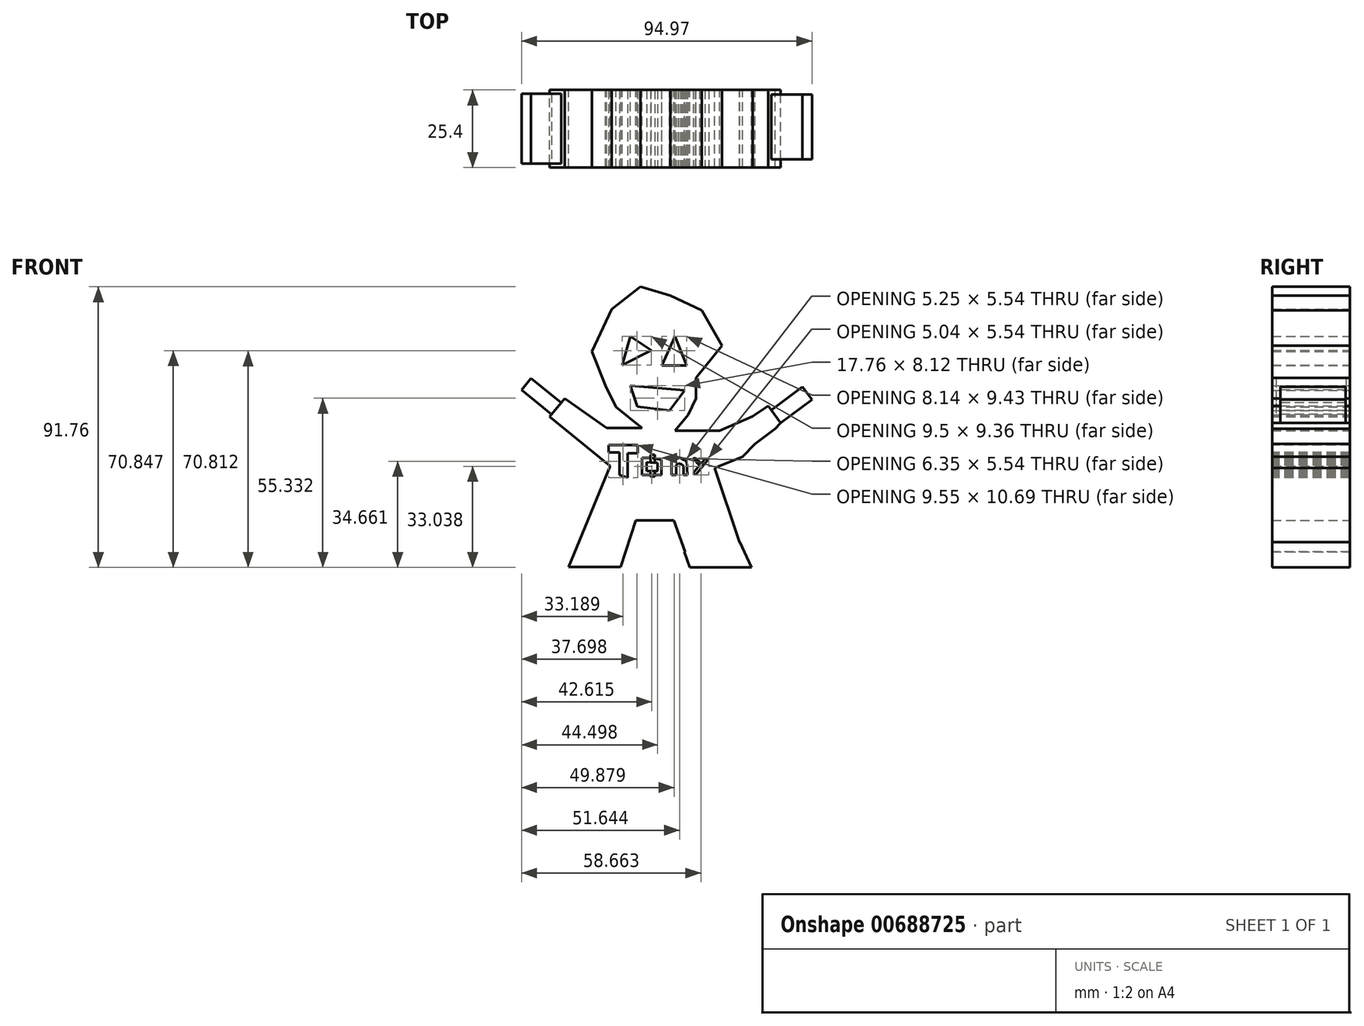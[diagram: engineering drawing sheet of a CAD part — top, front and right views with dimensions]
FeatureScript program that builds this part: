
annotation { "Feature Type Name" : "Feature", "Feature Type Description" : "" }
export const myFeature = defineFeature(function(context is Context, id is Id, definition is map)
    precondition{}
    {
        {
            var Q0;
            Q0=qCreatedBy(makeId("Front.planeOp"),FACE);
            var sketch = newSketch(context, id + "F0", { "sketchPlane" : qUnion([Q0])});
            skLineSegment(sketch, "E0.bottom", {"start": v(-60.07, 58.54) * mm, "end": v(66.93, 58.54) * mm});
            skLineSegment(sketch, "E0.top", {"start": v(-60.07, -68.46) * mm, "end": v(66.93, -68.46) * mm});
            skLineSegment(sketch, "E0.left", {"start": v(-60.07, 58.54) * mm, "end": v(-60.07, -68.46) * mm});
            skLineSegment(sketch, "E0.right", {"start": v(66.93, 58.54) * mm, "end": v(66.93, -68.46) * mm});
            skSolve(sketch);
        }
        {
            var Q0;
            Q0=makeQuery(id+"F0.imprint","IMPRINT",FACE,{"disambiguationData":[TD([[makeQuery(id+"F0.imprint","IMPRINT",EDGE,{"derivedFrom":sQuery(id+"F0.wireOp",EDGE,"E0.bottom")}),-1.0]])]});
            extrude(context, id + "F1", {"entities" : qUnion([Q0]), "depth" : 25.4 * mm, "offsetDistance" : 25.4 * mm});
        }
        {
            var Q0;
            Q0=makeQuery(id+"F1.opExtrude","CAP_FACE",FACE,{"disambiguationData":[OSD([sQuery(id+"F0.wireOp",EDGE,"E0.bottom"),sQuery(id+"F0.wireOp",EDGE,"E0.top"),sQuery(id+"F0.wireOp",EDGE,"E0.left"),sQuery(id+"F0.wireOp",EDGE,"E0.right")])],"isStart":false});
            var sketch = newSketch(context, id + "F2", { "sketchPlane" : qUnion([Q0])});
            skLineSegment(sketch, "E1", {"start": v(-30.9, -68.46) * mm, "end": v(-13.51, -26.26) * mm});
            skLineSegment(sketch, "E2", {"start": v(-13.51, -26.26) * mm, "end": v(-39.68, -4.87) * mm});
            skLineSegment(sketch, "E3", {"start": v(-39.68, -4.87) * mm, "end": v(-34.33, 0) * mm});
            skLineSegment(sketch, "E4", {"start": v(-34.33, 0) * mm, "end": v(-34.33, 2.58) * mm});
            skLineSegment(sketch, "E5", {"start": v(-34.33, 2.58) * mm, "end": v(-34.33, 6.2) * mm});
            skLineSegment(sketch, "E6", {"start": v(-34.33, 6.2) * mm, "end": v(-43.69, 6.2) * mm});
            skLineSegment(sketch, "E7", {"start": v(-43.69, 6.2) * mm, "end": v(-45.02, -5.82) * mm});
            skLineSegment(sketch, "E8", {"start": v(-45.02, -5.82) * mm, "end": v(-39.68, -6.02) * mm});
            skLineSegment(sketch, "E9", {"start": v(-34.33, 0) * mm, "end": v(-14.66, -13.84) * mm});
            skLineSegment(sketch, "E10", {"start": v(-14.66, -13.84) * mm, "end": v(-3.01, -13.84) * mm});
            skLineSegment(sketch, "E11", {"start": v(-3.01, -13.84) * mm, "end": v(-11.53, -6.88) * mm});
            skLineSegment(sketch, "E12", {"start": v(-11.53, -6.88) * mm, "end": v(-15.04, 0) * mm});
            skLineSegment(sketch, "E13", {"start": v(-15.04, 0) * mm, "end": v(-19.43, 11.17) * mm});
            skLineSegment(sketch, "E14", {"start": v(-19.43, 11.17) * mm, "end": v(-12.94, 25.11) * mm});
            skLineSegment(sketch, "E15", {"start": v(-12.94, 25.11) * mm, "end": v(-3.58, 32.37) * mm});
            skLineSegment(sketch, "E16", {"start": v(-3.58, 32.37) * mm, "end": v(6.15, 29.5) * mm});
            skLineSegment(sketch, "E17", {"start": v(6.15, 29.5) * mm, "end": v(16.48, 24.7) * mm});
            skLineSegment(sketch, "E18", {"start": v(16.48, 24.7) * mm, "end": v(23.15, 13.08) * mm});
            skLineSegment(sketch, "E19", {"start": v(23.15, 13.08) * mm, "end": v(14.54, 2.55) * mm});
            skLineSegment(sketch, "E20", {"start": v(14.54, 2.55) * mm, "end": v(14.54, -4.1) * mm});
            skLineSegment(sketch, "E21", {"start": v(14.54, -4.1) * mm, "end": v(12.02, -9.53) * mm});
            skLineSegment(sketch, "E22", {"start": v(12.02, -9.53) * mm, "end": v(7.75, -14.75) * mm});
            skLineSegment(sketch, "E23", {"start": v(7.75, -14.75) * mm, "end": v(22.38, -14.75) * mm});
            skLineSegment(sketch, "E24", {"start": v(22.38, -14.75) * mm, "end": v(33.08, -10.03) * mm});
            skLineSegment(sketch, "E25", {"start": v(33.08, -10.03) * mm, "end": v(38.23, -6.59) * mm});
            skLineSegment(sketch, "E26", {"start": v(38.23, -6.59) * mm, "end": v(41.35, -2.77) * mm});
            skLineSegment(sketch, "E27", {"start": v(41.35, -2.77) * mm, "end": v(41.29, 0) * mm});
            skLineSegment(sketch, "E28", {"start": v(41.29, 0) * mm, "end": v(45.32, 4.93) * mm});
            skLineSegment(sketch, "E29", {"start": v(45.32, 4.93) * mm, "end": v(50.4, 2.55) * mm});
            skLineSegment(sketch, "E30", {"start": v(50.4, 2.55) * mm, "end": v(51.6, -3.53) * mm});
            skLineSegment(sketch, "E31", {"start": v(51.6, -3.53) * mm, "end": v(50.65, -6.02) * mm});
            skLineSegment(sketch, "E32", {"start": v(50.65, -6.02) * mm, "end": v(45.87, -6.02) * mm});
            skLineSegment(sketch, "E33", {"start": v(45.87, -6.02) * mm, "end": v(43.78, -10.51) * mm});
            skLineSegment(sketch, "E34", {"start": v(43.78, -10.51) * mm, "end": v(40.53, -14.04) * mm});
            skLineSegment(sketch, "E35", {"start": v(40.53, -14.04) * mm, "end": v(33.84, -19) * mm});
            skLineSegment(sketch, "E36", {"start": v(33.84, -19) * mm, "end": v(29.83, -23.2) * mm});
            skLineSegment(sketch, "E37", {"start": v(29.83, -23.2) * mm, "end": v(20.67, -26.83) * mm});
            skLineSegment(sketch, "E38", {"start": v(20.67, -26.83) * mm, "end": v(34.6, -68.46) * mm});
            skLineSegment(sketch, "E39", {"start": v(34.6, -68.46) * mm, "end": v(16.27, -68.46) * mm});
            skLineSegment(sketch, "E40", {"start": v(16.27, -68.46) * mm, "end": v(7.3, -44.02) * mm});
            skLineSegment(sketch, "E41", {"start": v(7.3, -44.02) * mm, "end": v(-5.11, -44.02) * mm});
            skLineSegment(sketch, "E42", {"start": v(-5.11, -44.02) * mm, "end": v(-12.94, -68.46) * mm});
            skLineSegment(sketch, "E43", {"start": v(-12.94, -68.46) * mm, "end": v(-30.9, -68.46) * mm});
            skLineSegment(sketch, "E44", {"start": v(-33.24, -10.13) * mm, "end": v(-28.38, -4.19) * mm});
            skLineSegment(sketch, "E45", {"start": v(38.23, -6.59) * mm, "end": v(42.32, -12.09) * mm});
            skLineSegment(sketch, "E46", {"start": v(-27.12, -59.3) * mm, "end": v(-10, -59.3) * mm});
            skLineSegment(sketch, "E47", {"start": v(11.14, -54.46) * mm, "end": v(28.87, -51.34) * mm});
            skLineSegment(sketch, "E48", {"start": v(-19.2, -40.09) * mm, "end": v(25.1, -40.09) * mm});
            skLineSegment(sketch, "E49", {"start": v(-3.01, -13.84) * mm, "end": v(0, -18.8) * mm});
            skLineSegment(sketch, "E50", {"start": v(0, -18.8) * mm, "end": v(4.63, -18.8) * mm});
            skLineSegment(sketch, "E51", {"start": v(4.63, -18.8) * mm, "end": v(7.75, -14.75) * mm});
            skLineSegment(sketch, "E52", {"start": v(-6.83, 16.14) * mm, "end": v(-9.5, 6.78) * mm});
            skLineSegment(sketch, "E53", {"start": v(-9.5, 6.78) * mm, "end": v(0, 11.63) * mm});
            skLineSegment(sketch, "E54", {"start": v(0, 11.63) * mm, "end": v(-6.83, 16.14) * mm});
            skLineSegment(sketch, "E55", {"start": v(7.75, 16.14) * mm, "end": v(3.36, 6.7) * mm});
            skLineSegment(sketch, "E56", {"start": v(3.36, 6.7) * mm, "end": v(11.5, 6.7) * mm});
            skLineSegment(sketch, "E57", {"start": v(11.5, 6.7) * mm, "end": v(7.75, 16.14) * mm});
            skLineSegment(sketch, "E58", {"start": v(-6.83, 0) * mm, "end": v(10.93, -1.43) * mm});
            skLineSegment(sketch, "E59", {"start": v(10.93, -1.43) * mm, "end": v(5.96, -8.12) * mm});
            skLineSegment(sketch, "E60", {"start": v(5.96, -8.12) * mm, "end": v(-4.54, -6.78) * mm});
            skLineSegment(sketch, "E61", {"start": v(-4.54, -6.78) * mm, "end": v(-6.83, 0) * mm});
            skLineSegment(sketch, "E62", {"start": v(-9.5, -22.06) * mm, "end": v(-9.5, -33.51) * mm});
            skLineSegment(sketch, "E63", {"start": v(-9.5, -33.51) * mm, "end": v(-9.5, -22.06) * mm});
            skLineSegment(sketch, "E64", {"start": v(-3.01, -22.06) * mm, "end": v(-15.8, -22.06) * mm});
            skLineSegment(sketch, "E65", {"start": v(1.95, -25.87) * mm, "end": v(-3.4, -25.87) * mm});
            skLineSegment(sketch, "E66", {"start": v(-3.4, -25.87) * mm, "end": v(-3.4, -32.75) * mm});
            skLineSegment(sketch, "E67", {"start": v(-3.4, -32.75) * mm, "end": v(1.76, -32.75) * mm});
            skLineSegment(sketch, "E68", {"start": v(1.76, -32.75) * mm, "end": v(1.95, -25.87) * mm});
            skLineSegment(sketch, "E69", {"start": v(5.96, -32.75) * mm, "end": v(5.96, -22.06) * mm});
            skLineSegment(sketch, "E70", {"start": v(5.96, -22.06) * mm, "end": v(10.35, -34.28) * mm});
            skLineSegment(sketch, "E71", {"start": v(10.35, -34.28) * mm, "end": v(10.35, -22.06) * mm});
            skLineSegment(sketch, "E72", {"start": v(14.17, -23.2) * mm, "end": v(16.64, -29.43) * mm});
            skLineSegment(sketch, "E73", {"start": v(16.64, -29.43) * mm, "end": v(19.14, -22.44) * mm});
            skLineSegment(sketch, "E74", {"start": v(19.14, -22.44) * mm, "end": v(16.64, -29.43) * mm});
            skLineSegment(sketch, "E75", {"start": v(16.64, -37.52) * mm, "end": v(16.64, -29.43) * mm});
            skSolve(sketch);
        }
        {
            var Q0;
            Q0=makeQuery(id+"F2.imprint","IMPRINT",FACE,{"disambiguationData":[TD([[makeQuery(id+"F2.imprint","IMPRINT",EDGE,{"derivedFrom":sQuery(id+"F2.wireOp",EDGE,"E11")}),-1.0]])]});
            var Q1;
            {var subQ7=sQuery(id+"F2.wireOp",EDGE,"E10");Q1=makeQuery(id+"F2.imprint","IMPRINT",FACE,{"disambiguationData":[TD([[makeQuery(id+"F2.imprint","IMPRINT",EDGE,{"derivedFrom":subQ7}),-1.0]])]});}
            var Q2;
            Q2=makeQuery(id+"F2.imprint","IMPRINT",FACE,{"disambiguationData":[TD([[makeQuery(id+"F2.imprint","IMPRINT",EDGE,{"derivedFrom":sQuery(id+"F2.wireOp",EDGE,"E65")}),1.0]])]});
            var Q3;
            {var subQ0=sQuery(id+"F2.wireOp",EDGE,"E41");Q3=makeQuery(id+"F2.imprint","IMPRINT",FACE,{"disambiguationData":[TD([[makeQuery(id+"F2.imprint","IMPRINT",EDGE,{"derivedFrom":subQ0}),-1.0]])]});}
            extrude(context, id + "F3", {"entities" : qUnion([Q0, Q1, Q2, Q3]), "operationType" : NewBodyOperationType.ADD, "depth" : 25.4 * mm, "offsetDistance" : 25.4 * mm});
        }
        {
            var Q0;
            {var subQ0=sQuery(id+"F0.wireOp",EDGE,"E0.top");var subQ1=sQuery(id+"F0.wireOp",EDGE,"E0.right");var subQ2=sQuery(id+"F0.wireOp",EDGE,"E0.bottom");var subQ3=sQuery(id+"F0.wireOp",EDGE,"E0.left");Q0=makeQuery(id+"F3.boolean.opBoolean","SPLIT",FACE,{"disambiguationData":[TD([makeQuery(id+"F1.opExtrude","SWEPT_FACE",FACE,{"disambiguationData":[OSD([subQ2])]})])],"derivedFrom":makeQuery(id+"F1.opExtrude","CAP_FACE",FACE,{"disambiguationData":[OSD([subQ2,subQ0,subQ3,subQ1])],"isStart":false})});}
            var sketch = newSketch(context, id + "F4", { "sketchPlane" : qUnion([Q0])});
            skLineSegment(sketch, "E76.bottom", {"start": v(-60.07, 58.54) * mm, "end": v(66.93, 58.54) * mm});
            skLineSegment(sketch, "E76.top", {"start": v(-60.07, -68.46) * mm, "end": v(66.93, -68.46) * mm});
            skLineSegment(sketch, "E76.left", {"start": v(-60.07, 58.54) * mm, "end": v(-60.07, -68.46) * mm});
            skLineSegment(sketch, "E76.right", {"start": v(66.93, 58.54) * mm, "end": v(66.93, -68.46) * mm});
            skSolve(sketch);
        }
        {
            var Q0;
            Q0 = qSketchRegion(id + "F4", true);
            extrude(context, id + "F5", {"entities" : qUnion([Q0]), "operationType" : NewBodyOperationType.REMOVE, "oppositeDirection" : true, "depth" : 25.4 * mm, "offsetDistance" : 25.4 * mm});
        }
        {
            var Q0;
            Q0=makeQuery(id+"F3.opExtrude","SWEPT_FACE",FACE,{"disambiguationData":[OSD([sQuery(id+"F2.wireOp",EDGE,"E44")])]});
            var sketch = newSketch(context, id + "F6", { "sketchPlane" : qUnion([Q0])});
            skSolve(sketch);
        }
        {
            var Q0;
            Q0=makeQuery(id+"F3.opExtrude","SWEPT_FACE",FACE,{"disambiguationData":[OSD([sQuery(id+"F2.wireOp",EDGE,"E45")])]});
            var sketch = newSketch(context, id + "F7", { "sketchPlane" : qUnion([Q0])});
            skLineSegment(sketch, "E77.bottom", {"start": v(-48.1, -29.78) * mm, "end": v(-26.82, -29.78) * mm});
            skLineSegment(sketch, "E77.top", {"start": v(-48.1, -34.94) * mm, "end": v(-26.82, -34.94) * mm});
            skLineSegment(sketch, "E77.left", {"start": v(-48.1, -29.78) * mm, "end": v(-48.1, -34.94) * mm});
            skLineSegment(sketch, "E77.right", {"start": v(-26.82, -29.78) * mm, "end": v(-26.82, -34.94) * mm});
            skSolve(sketch);
        }
        {
            var Q0;
            Q0 = qSketchRegion(id + "F7", true);
            extrude(context, id + "F8", {"entities" : qUnion([Q0]), "operationType" : NewBodyOperationType.ADD, "depth" : 12.7 * mm, "offsetDistance" : 25.4 * mm});
        }
        {
            var Q0;
            Q0=qCreatedBy(makeId("Front.planeOp"),FACE);
            var sketch = newSketch(context, id + "F9", { "sketchPlane" : qUnion([Q0])});
            skLineSegment(sketch, "E78", {"start": v(10.79, -54.35) * mm, "end": v(12.6, -59.4) * mm});
            skLineSegment(sketch, "E79", {"start": v(12.6, -59.4) * mm, "end": v(32.76, -59.4) * mm});
            skLineSegment(sketch, "E80", {"start": v(32.76, -59.4) * mm, "end": v(28.93, -51.13) * mm});
            skLineSegment(sketch, "E81", {"start": v(28.93, -51.13) * mm, "end": v(10.79, -54.35) * mm});
            skSolve(sketch);
        }
        {
            var Q0;
            Q0=makeQuery(id+"F9.imprint","IMPRINT",FACE,{"disambiguationData":[TD([[makeQuery(id+"F9.imprint","IMPRINT",EDGE,{"derivedFrom":sQuery(id+"F9.wireOp",EDGE,"E78")}),1.0]])]});
            extrude(context, id + "F10", {"entities" : qUnion([Q0]), "operationType" : NewBodyOperationType.ADD, "depth" : 50.8 * mm, "offsetDistance" : 25.4 * mm});
        }
        {
            var Q0;
            Q0=makeQuery(id+"F10.opExtrude","CAP_FACE",FACE,{"disambiguationData":[OSD([sQuery(id+"F9.wireOp",EDGE,"E78"),sQuery(id+"F9.wireOp",EDGE,"E79"),sQuery(id+"F9.wireOp",EDGE,"E80"),sQuery(id+"F9.wireOp",EDGE,"E81")])],"isStart":true});
            extrude(context, id + "F11", {"entities" : qUnion([Q0]), "operationType" : NewBodyOperationType.REMOVE, "oppositeDirection" : true, "depth" : 25.4 * mm, "offsetDistance" : 25.4 * mm});
        }
        {
            var Q0;
            Q0=makeQuery(id+"F10.boolean.opBoolean","MERGE",FACE,{"derivedFrom":[makeQuery(id+"F3.opExtrude","CAP_FACE",FACE,{"disambiguationData":[OSD([sQuery(id+"F2.wireOp",EDGE,"E1"),sQuery(id+"F2.wireOp",EDGE,"E2"),sQuery(id+"F2.wireOp",EDGE,"E9"),sQuery(id+"F2.wireOp",EDGE,"E10"),sQuery(id+"F2.wireOp",EDGE,"E11"),sQuery(id+"F2.wireOp",EDGE,"E12"),sQuery(id+"F2.wireOp",EDGE,"E13"),sQuery(id+"F2.wireOp",EDGE,"E14"),sQuery(id+"F2.wireOp",EDGE,"E15"),sQuery(id+"F2.wireOp",EDGE,"E16"),sQuery(id+"F2.wireOp",EDGE,"E17"),sQuery(id+"F2.wireOp",EDGE,"E18"),sQuery(id+"F2.wireOp",EDGE,"E19"),sQuery(id+"F2.wireOp",EDGE,"E20"),sQuery(id+"F2.wireOp",EDGE,"E21"),sQuery(id+"F2.wireOp",EDGE,"E22"),sQuery(id+"F2.wireOp",EDGE,"E23"),sQuery(id+"F2.wireOp",EDGE,"E24"),sQuery(id+"F2.wireOp",EDGE,"E25"),sQuery(id+"F2.wireOp",EDGE,"E34"),sQuery(id+"F2.wireOp",EDGE,"E35"),sQuery(id+"F2.wireOp",EDGE,"E36"),sQuery(id+"F2.wireOp",EDGE,"E37"),sQuery(id+"F2.wireOp",EDGE,"E38"),sQuery(id+"F2.wireOp",EDGE,"E40"),sQuery(id+"F2.wireOp",EDGE,"E41"),sQuery(id+"F2.wireOp",EDGE,"E42"),sQuery(id+"F2.wireOp",EDGE,"E44"),sQuery(id+"F2.wireOp",EDGE,"E45"),sQuery(id+"F2.wireOp",EDGE,"E46"),sQuery(id+"F2.wireOp",EDGE,"E47"),sQuery(id+"F2.wireOp",EDGE,"E52"),sQuery(id+"F2.wireOp",EDGE,"E53"),sQuery(id+"F2.wireOp",EDGE,"E54"),sQuery(id+"F2.wireOp",EDGE,"E55"),sQuery(id+"F2.wireOp",EDGE,"E56"),sQuery(id+"F2.wireOp",EDGE,"E57"),sQuery(id+"F2.wireOp",EDGE,"E58"),sQuery(id+"F2.wireOp",EDGE,"E59"),sQuery(id+"F2.wireOp",EDGE,"E60"),sQuery(id+"F2.wireOp",EDGE,"E61")])],"isStart":false}),makeQuery(id+"F10.opExtrude","CAP_FACE",FACE,{"disambiguationData":[OSD([sQuery(id+"F9.wireOp",EDGE,"E78"),sQuery(id+"F9.wireOp",EDGE,"E79"),sQuery(id+"F9.wireOp",EDGE,"E80"),sQuery(id+"F9.wireOp",EDGE,"E81")])],"isStart":false})]});
            var sketch = newSketch(context, id + "F12", { "sketchPlane" : qUnion([Q0])});
            skLineSegment(sketch, "E82", {"start": v(-10.4, -29.12) * mm, "end": v(-10.4, -21.86) * mm});
            skLineSegment(sketch, "E83", {"start": v(-10.4, -21.86) * mm, "end": v(-14.04, -21.86) * mm});
            skLineSegment(sketch, "E84", {"start": v(-14.04, -21.86) * mm, "end": v(-14.04, -19.38) * mm});
            skLineSegment(sketch, "E85", {"start": v(-14.04, -19.38) * mm, "end": v(-4.49, -19.38) * mm});
            skLineSegment(sketch, "E86", {"start": v(-4.49, -19.38) * mm, "end": v(-4.49, -22.06) * mm});
            skLineSegment(sketch, "E87", {"start": v(-4.49, -22.06) * mm, "end": v(-7.73, -22.06) * mm});
            skLineSegment(sketch, "E88", {"start": v(-7.73, -22.06) * mm, "end": v(-7.73, -30.08) * mm});
            skLineSegment(sketch, "E89", {"start": v(-7.73, -30.08) * mm, "end": v(-10.4, -29.12) * mm});
            skLineSegment(sketch, "E90", {"start": v(0, -23.58) * mm, "end": v(-3.01, -23.58) * mm});
            skLineSegment(sketch, "E91", {"start": v(-3.01, -23.58) * mm, "end": v(-3.01, -29.12) * mm});
            skLineSegment(sketch, "E92", {"start": v(-3.01, -29.12) * mm, "end": v(3.34, -29.12) * mm});
            skLineSegment(sketch, "E93", {"start": v(3.34, -29.12) * mm, "end": v(3.34, -24.16) * mm});
            skLineSegment(sketch, "E94", {"start": v(3.34, -24.16) * mm, "end": v(0, -23.58) * mm});
            skLineSegment(sketch, "E95", {"start": v(-1.56, -24.96) * mm, "end": v(-1.56, -27.93) * mm});
            skLineSegment(sketch, "E96", {"start": v(-1.56, -27.93) * mm, "end": v(2, -27.93) * mm});
            skLineSegment(sketch, "E97", {"start": v(2, -27.93) * mm, "end": v(2, -25.29) * mm});
            skLineSegment(sketch, "E98", {"start": v(2, -25.29) * mm, "end": v(-1.56, -24.96) * mm});
            skLineSegment(sketch, "E99", {"start": v(6.57, -29.12) * mm, "end": v(6.57, -23.58) * mm});
            skLineSegment(sketch, "E100", {"start": v(6.57, -23.58) * mm, "end": v(7.56, -23.58) * mm});
            skLineSegment(sketch, "E101", {"start": v(7.56, -23.58) * mm, "end": v(7.56, -24.64) * mm});
            skLineSegment(sketch, "E102", {"start": v(7.56, -24.64) * mm, "end": v(8.02, -24.16) * mm});
            skLineSegment(sketch, "E103", {"start": v(8.02, -24.16) * mm, "end": v(8.78, -23.58) * mm});
            skLineSegment(sketch, "E104", {"start": v(8.78, -23.58) * mm, "end": v(9.55, -23.58) * mm});
            skLineSegment(sketch, "E105", {"start": v(9.55, -23.58) * mm, "end": v(10.32, -24.16) * mm});
            skLineSegment(sketch, "E106", {"start": v(10.32, -24.16) * mm, "end": v(11.03, -24.33) * mm});
            skLineSegment(sketch, "E107", {"start": v(11.03, -24.33) * mm, "end": v(11.48, -24.96) * mm});
            skLineSegment(sketch, "E108", {"start": v(11.48, -24.96) * mm, "end": v(11.68, -25.94) * mm});
            skLineSegment(sketch, "E109", {"start": v(11.68, -25.94) * mm, "end": v(11.68, -27.6) * mm});
            skLineSegment(sketch, "E110", {"start": v(11.68, -27.6) * mm, "end": v(11.82, -28.41) * mm});
            skLineSegment(sketch, "E111", {"start": v(11.82, -28.41) * mm, "end": v(11.82, -29.12) * mm});
            skLineSegment(sketch, "E112", {"start": v(11.82, -29.12) * mm, "end": v(10.57, -29.12) * mm});
            skLineSegment(sketch, "E113", {"start": v(10.57, -29.12) * mm, "end": v(10.57, -26.26) * mm});
            skLineSegment(sketch, "E114", {"start": v(10.57, -26.26) * mm, "end": v(9.8, -25.63) * mm});
            skLineSegment(sketch, "E115", {"start": v(9.8, -25.63) * mm, "end": v(8.81, -25.32) * mm});
            skLineSegment(sketch, "E116", {"start": v(8.81, -25.32) * mm, "end": v(8.16, -25.94) * mm});
            skLineSegment(sketch, "E117", {"start": v(8.16, -25.94) * mm, "end": v(8.16, -29.12) * mm});
            skLineSegment(sketch, "E118", {"start": v(8.16, -29.12) * mm, "end": v(6.57, -29.12) * mm});
            skLineSegment(sketch, "E119", {"start": v(13.7, -23.87) * mm, "end": v(15.68, -25.97) * mm});
            skLineSegment(sketch, "E120", {"start": v(15.68, -25.97) * mm, "end": v(13.7, -28.47) * mm});
            skLineSegment(sketch, "E121", {"start": v(13.7, -28.47) * mm, "end": v(14.51, -29.12) * mm});
            skLineSegment(sketch, "E122", {"start": v(14.51, -29.12) * mm, "end": v(18.73, -23.81) * mm});
            skLineSegment(sketch, "E123", {"start": v(18.73, -23.81) * mm, "end": v(17.53, -23.81) * mm});
            skLineSegment(sketch, "E124", {"start": v(17.53, -23.81) * mm, "end": v(16.4, -25.5) * mm});
            skLineSegment(sketch, "E125", {"start": v(16.4, -25.5) * mm, "end": v(14.35, -23.58) * mm});
            skLineSegment(sketch, "E126", {"start": v(14.35, -23.58) * mm, "end": v(13.7, -23.87) * mm});
            skSolve(sketch);
        }
        {
            var Q0;
            Q0=makeQuery(id+"F12.imprint","IMPRINT",FACE,{"disambiguationData":[TD([[makeQuery(id+"F12.imprint","IMPRINT",EDGE,{"derivedFrom":sQuery(id+"F12.wireOp",EDGE,"E82")}),-1.0]])]});
            var Q1;
            Q1=makeQuery(id+"F12.imprint","IMPRINT",FACE,{"disambiguationData":[TD([[makeQuery(id+"F12.imprint","IMPRINT",EDGE,{"derivedFrom":sQuery(id+"F12.wireOp",EDGE,"E90")}),1.0]])]});
            var Q2;
            Q2=makeQuery(id+"F12.imprint","IMPRINT",FACE,{"disambiguationData":[TD([[makeQuery(id+"F12.imprint","IMPRINT",EDGE,{"derivedFrom":sQuery(id+"F12.wireOp",EDGE,"E99")}),-1.0]])]});
            var Q3;
            Q3=makeQuery(id+"F12.imprint","IMPRINT",FACE,{"disambiguationData":[TD([[makeQuery(id+"F12.imprint","IMPRINT",EDGE,{"derivedFrom":sQuery(id+"F12.wireOp",EDGE,"E119")}),1.0]])]});
            extrude(context, id + "F13", {"entities" : qUnion([Q0, Q1, Q2, Q3]), "operationType" : NewBodyOperationType.REMOVE, "oppositeDirection" : true, "depth" : 25.4 * mm, "offsetDistance" : 25.4 * mm});
        }
        {
            var Q0;
            Q0=makeQuery(id+"F13.boolean.opBoolean","SPLIT",FACE,{"disambiguationData":[TD([makeQuery(id+"F13.opExtrude","SWEPT_FACE",FACE,{"disambiguationData":[OSD([sQuery(id+"F12.wireOp",EDGE,"E95")])]})])],"derivedFrom":makeQuery(id+"F10.boolean.opBoolean","MERGE",FACE,{"derivedFrom":[makeQuery(id+"F3.opExtrude","CAP_FACE",FACE,{"disambiguationData":[OSD([sQuery(id+"F2.wireOp",EDGE,"E1"),sQuery(id+"F2.wireOp",EDGE,"E2"),sQuery(id+"F2.wireOp",EDGE,"E9"),sQuery(id+"F2.wireOp",EDGE,"E10"),sQuery(id+"F2.wireOp",EDGE,"E11"),sQuery(id+"F2.wireOp",EDGE,"E12"),sQuery(id+"F2.wireOp",EDGE,"E13"),sQuery(id+"F2.wireOp",EDGE,"E14"),sQuery(id+"F2.wireOp",EDGE,"E15"),sQuery(id+"F2.wireOp",EDGE,"E16"),sQuery(id+"F2.wireOp",EDGE,"E17"),sQuery(id+"F2.wireOp",EDGE,"E18"),sQuery(id+"F2.wireOp",EDGE,"E19"),sQuery(id+"F2.wireOp",EDGE,"E20"),sQuery(id+"F2.wireOp",EDGE,"E21"),sQuery(id+"F2.wireOp",EDGE,"E22"),sQuery(id+"F2.wireOp",EDGE,"E23"),sQuery(id+"F2.wireOp",EDGE,"E24"),sQuery(id+"F2.wireOp",EDGE,"E25"),sQuery(id+"F2.wireOp",EDGE,"E34"),sQuery(id+"F2.wireOp",EDGE,"E35"),sQuery(id+"F2.wireOp",EDGE,"E36"),sQuery(id+"F2.wireOp",EDGE,"E37"),sQuery(id+"F2.wireOp",EDGE,"E38"),sQuery(id+"F2.wireOp",EDGE,"E40"),sQuery(id+"F2.wireOp",EDGE,"E41"),sQuery(id+"F2.wireOp",EDGE,"E42"),sQuery(id+"F2.wireOp",EDGE,"E44"),sQuery(id+"F2.wireOp",EDGE,"E45"),sQuery(id+"F2.wireOp",EDGE,"E46"),sQuery(id+"F2.wireOp",EDGE,"E47"),sQuery(id+"F2.wireOp",EDGE,"E52"),sQuery(id+"F2.wireOp",EDGE,"E53"),sQuery(id+"F2.wireOp",EDGE,"E54"),sQuery(id+"F2.wireOp",EDGE,"E55"),sQuery(id+"F2.wireOp",EDGE,"E56"),sQuery(id+"F2.wireOp",EDGE,"E57"),sQuery(id+"F2.wireOp",EDGE,"E58"),sQuery(id+"F2.wireOp",EDGE,"E59"),sQuery(id+"F2.wireOp",EDGE,"E60"),sQuery(id+"F2.wireOp",EDGE,"E61")])],"isStart":false}),makeQuery(id+"F10.opExtrude","CAP_FACE",FACE,{"disambiguationData":[OSD([sQuery(id+"F9.wireOp",EDGE,"E78"),sQuery(id+"F9.wireOp",EDGE,"E79"),sQuery(id+"F9.wireOp",EDGE,"E80"),sQuery(id+"F9.wireOp",EDGE,"E81")])],"isStart":false})]})});
            var sketch = newSketch(context, id + "F14", { "sketchPlane" : qUnion([Q0])});
            skLineSegment(sketch, "E127", {"start": v(-0.27, -29.08) * mm, "end": v(-0.27, -22.56) * mm});
            skLineSegment(sketch, "E128", {"start": v(-0.27, -22.56) * mm, "end": v(1.1, -22.56) * mm});
            skLineSegment(sketch, "E129", {"start": v(1.1, -22.56) * mm, "end": v(1.1, -29.7) * mm});
            skLineSegment(sketch, "E130", {"start": v(1.1, -29.7) * mm, "end": v(-0.29, -29.7) * mm});
            skLineSegment(sketch, "E131", {"start": v(-0.29, -29.7) * mm, "end": v(-0.27, -29.08) * mm});
            skSolve(sketch);
        }
        {
            var Q0;
            {var subQ0=sQuery(id+"F14.wireOp",EDGE,"E128");Q0=makeQuery(id+"F14.imprint","IMPRINT",FACE,{"disambiguationData":[TD([[makeQuery(id+"F14.imprint","IMPRINT",EDGE,{"derivedFrom":subQ0}),-1.0]])]});}
            var Q1;
            {var subQ1=sQuery(id+"F14.wireOp",EDGE,"E130");Q1=makeQuery(id+"F14.imprint","IMPRINT",FACE,{"disambiguationData":[TD([[makeQuery(id+"F14.imprint","IMPRINT",EDGE,{"derivedFrom":subQ1}),-1.0]])]});}
            extrude(context, id + "F15", {"entities" : qUnion([Q0, Q1]), "oppositeDirection" : true, "depth" : 25.4 * mm, "offsetDistance" : 25.4 * mm});
        }
        {
            var Q0;
            {var subQ0=sQuery(id+"F2.wireOp",EDGE,"E44");Q0=makeQuery(id+"F6.imprint","IMPRINT",FACE,{"disambiguationData":[TD([[makeQuery(id+"F6.imprint","IMPRINT",EDGE,{"derivedFrom":makeQuery(id+"F3.opExtrude","CAP_EDGE",EDGE,{"disambiguationData":[OSD([subQ0])],"isStart":false})}),1.0]])]});}
            var sketch = newSketch(context, id + "F16", { "sketchPlane" : qUnion([Q0])});
            skLineSegment(sketch, "E132.bottom", {"start": v(26.6, -23.02) * mm, "end": v(49.5, -23.02) * mm});
            skLineSegment(sketch, "E132.top", {"start": v(26.6, -27.9) * mm, "end": v(49.5, -27.9) * mm});
            skLineSegment(sketch, "E132.left", {"start": v(26.6, -23.02) * mm, "end": v(26.6, -27.9) * mm});
            skLineSegment(sketch, "E132.right", {"start": v(49.5, -23.02) * mm, "end": v(49.5, -27.9) * mm});
            skSolve(sketch);
        }
        {
            var Q0;
            Q0=makeQuery(id+"F16.imprint","IMPRINT",FACE,{"disambiguationData":[TD([[makeQuery(id+"F16.imprint","IMPRINT",EDGE,{"derivedFrom":sQuery(id+"F16.wireOp",EDGE,"E132.bottom")}),-1.0]])]});
            extrude(context, id + "F17", {"entities" : qUnion([Q0]), "operationType" : NewBodyOperationType.ADD, "depth" : 12.7 * mm, "offsetDistance" : 25.4 * mm});
        }
    });
